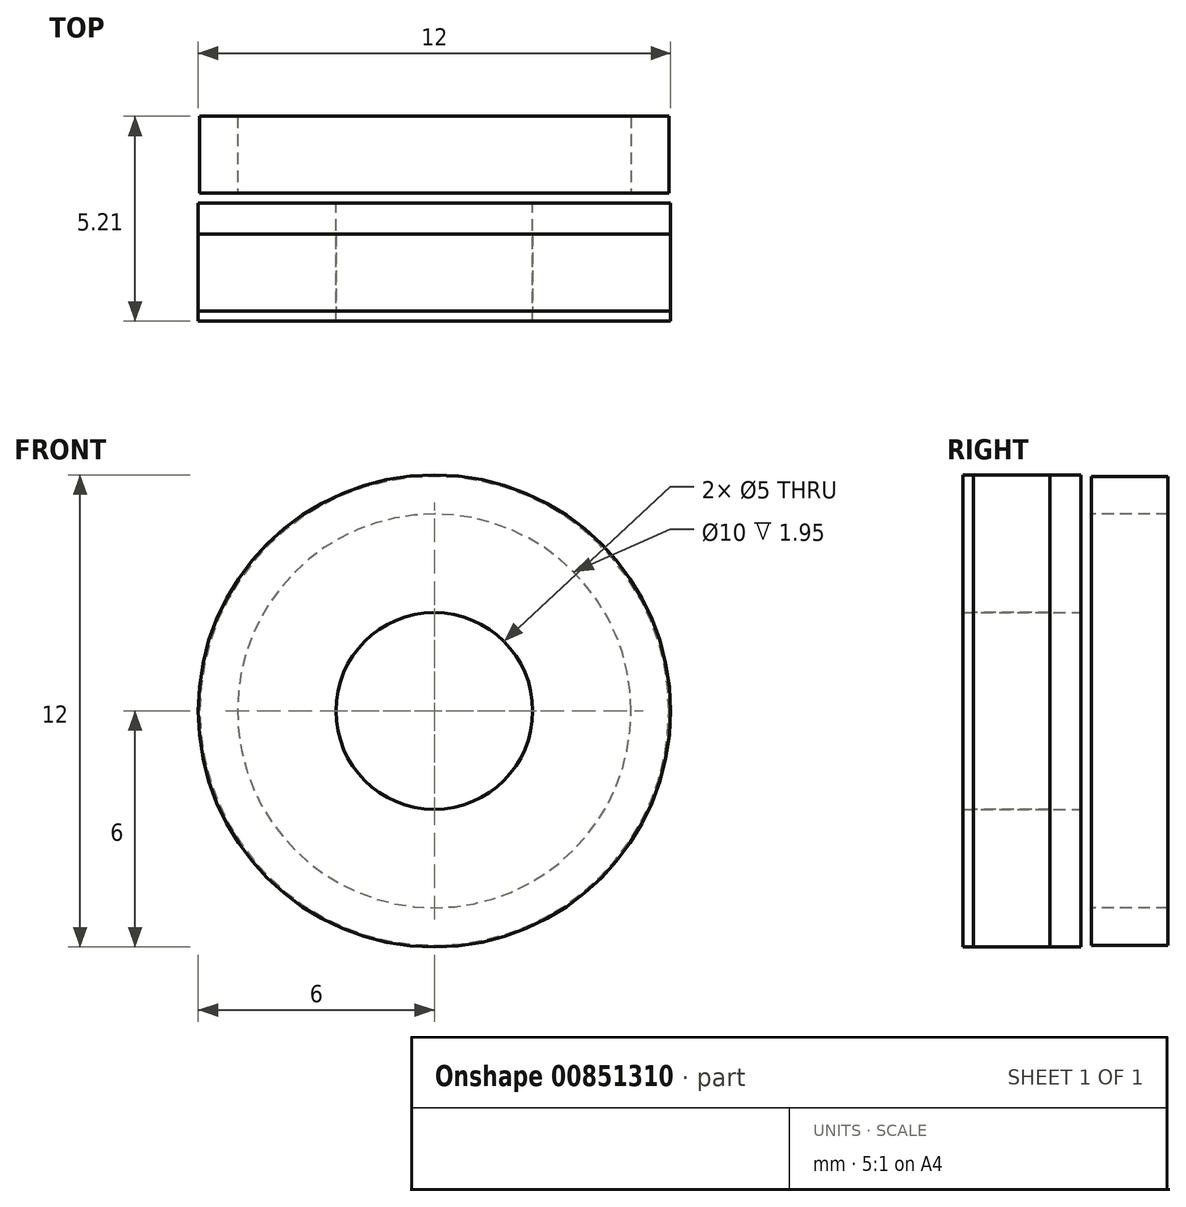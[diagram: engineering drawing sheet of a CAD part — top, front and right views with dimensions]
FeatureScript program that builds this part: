
annotation { "Feature Type Name" : "Feature", "Feature Type Description" : "" }
export const myFeature = defineFeature(function(context is Context, id is Id, definition is map)
    precondition{}
    {
        {
            var Q0;
            Q0=qCreatedBy(makeId("Front.planeOp"),FACE);
            var sketch = newSketch(context, id + "F0", { "sketchPlane" : qUnion([Q0])});
            skCircle(sketch, "E0", {"center": v(0, 0) * mm, "radius": 6 * mm});
            skCircle(sketch, "E1", {"center": v(0, 0) * mm, "radius": 5 * mm});
            skCircle(sketch, "E2", {"center": v(0, 0) * mm, "radius": 2.5 * mm});
            skSolve(sketch);
        }
        {
            var Q0;
            Q0=makeQuery(id+"F0.imprint","IMPRINT",FACE,{"disambiguationData":[TD([[makeQuery(id+"F0.imprint","IMPRINT",EDGE,{"derivedFrom":sQuery(id+"F0.wireOp",EDGE,"E1")}),1.0]])]});
            var Q1;
            Q1=makeQuery(id+"F0.imprint","IMPRINT",FACE,{"disambiguationData":[TD([[makeQuery(id+"F0.imprint","IMPRINT",EDGE,{"derivedFrom":sQuery(id+"F0.wireOp",EDGE,"E0")}),1.0]])]});
            extrude(context, id + "F1", {"entities" : qUnion([Q0, Q1]), "depth" : 3 * mm, "offsetDistance" : 25 * mm});
        }
        {
            var Q0;
            Q0=makeQuery(id+"F1.opExtrude","CAP_FACE",FACE,{"disambiguationData":[OSD([sQuery(id+"F0.wireOp",EDGE,"E0"),sQuery(id+"F0.wireOp",EDGE,"E2")])],"isStart":true});
            var sketch = newSketch(context, id + "F2", { "sketchPlane" : qUnion([Q0])});
            skCircle(sketch, "E3", {"center": v(0, 0) * mm, "radius": 5 * mm});
            skCircle(sketch, "E4", {"center": v(0, 0) * mm, "radius": 5.96 * mm});
            skSolve(sketch);
        }
        {
            var Q0;
            Q0=makeQuery(id+"F1.opExtrude","CAP_FACE",FACE,{"disambiguationData":[OSD([sQuery(id+"F0.wireOp",EDGE,"E0"),sQuery(id+"F0.wireOp",EDGE,"E2")])],"isStart":false});
            var Q1;
            Q1=makeQuery(id+"F2.imprint","IMPRINT",FACE,{"disambiguationData":[TD([[makeQuery(id+"F2.imprint","IMPRINT",EDGE,{"derivedFrom":sQuery(id+"F2.wireOp",EDGE,"E3")}),-1.0]])]});
            extrude(context, id + "F3", {"entities" : qUnion([Q0, Q1]), "oppositeDirection" : true, "depth" : 2.2 * mm, "offsetDistance" : 25 * mm, "hasSecondDirection" : true, "secondDirectionOppositeDirection" : true, "secondDirectionDepth" : 0.26 * mm});
        }
    });
